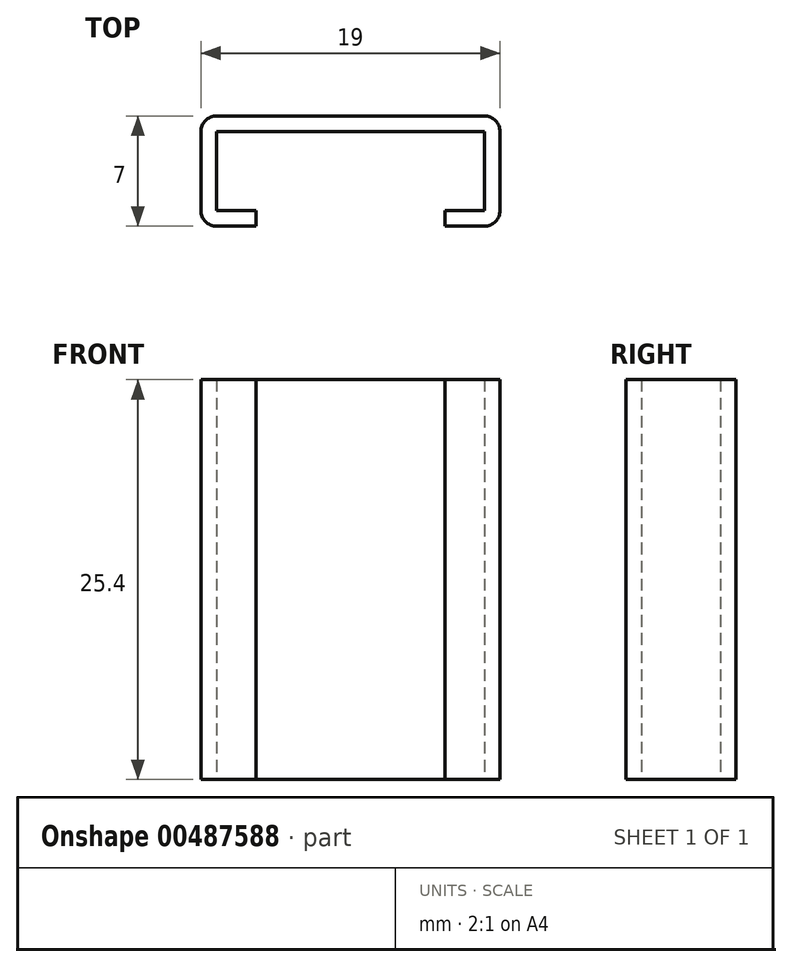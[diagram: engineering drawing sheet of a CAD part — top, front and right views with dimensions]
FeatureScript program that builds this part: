
annotation { "Feature Type Name" : "Feature", "Feature Type Description" : "" }
export const myFeature = defineFeature(function(context is Context, id is Id, definition is map)
    precondition{}
    {
        {
            var Q0;
            Q0=qCreatedBy(makeId("Top.planeOp"),FACE);
            var sketch = newSketch(context, id + "F0", { "sketchPlane" : qUnion([Q0])});
            skLineSegment(sketch, "E0", {"start": v(0, 0) * mm, "end": v(-8.5, 0) * mm});
            skLineSegment(sketch, "E1", {"start": v(-8.5, 0) * mm, "end": v(-8.5, -5) * mm});
            skLineSegment(sketch, "E2", {"start": v(-8.5, -5) * mm, "end": v(-6, -5) * mm});
            skLineSegment(sketch, "E3", {"start": v(0, 0) * mm, "end": v(0, 1) * mm});
            skLineSegment(sketch, "E4", {"start": v(0, 1) * mm, "end": v(-9.5, 1) * mm});
            skLineSegment(sketch, "E5", {"start": v(-9.5, 1) * mm, "end": v(-9.5, -6) * mm});
            skLineSegment(sketch, "E6", {"start": v(-9.5, -6) * mm, "end": v(-6, -6) * mm});
            skLineSegment(sketch, "E7", {"start": v(-6, -6) * mm, "end": v(-6, -5) * mm});
            skLineSegment(sketch, "E8.MirrorCS", {"start": v(9.5, 1) * mm, "end": v(9.5, -6) * mm});
            skLineSegment(sketch, "E9.MirrorCS", {"start": v(8.5, -5) * mm, "end": v(6, -5) * mm});
            skLineSegment(sketch, "E10.MirrorCS", {"start": v(0, 0) * mm, "end": v(8.5, 0) * mm});
            skLineSegment(sketch, "E11.MirrorCS", {"start": v(6, -6) * mm, "end": v(6, -5) * mm});
            skLineSegment(sketch, "E12.MirrorCS", {"start": v(0, 1) * mm, "end": v(9.5, 1) * mm});
            skLineSegment(sketch, "E13.MirrorCS", {"start": v(9.5, -6) * mm, "end": v(6, -6) * mm});
            skLineSegment(sketch, "E14.MirrorCS", {"start": v(8.5, 0) * mm, "end": v(8.5, -5) * mm});
            skSolve(sketch);
        }
        {
            var Q0;
            Q0=qSketchRegion(id+"F0",true);
            extrude(context, id + "F1", {"entities" : qUnion([Q0]), "depth" : 25.4 * mm});
        }
        {
            var Q0;
            Q0=makeQuery(id+"F1.opExtrude","SWEPT_EDGE",EDGE,{"disambiguationData":[OSD([sQuery(id+"F0.wireOp",EDGE,"E4"),sQuery(id+"F0.wireOp",EDGE,"E5")])]});
            var Q1;
            Q1=makeQuery(id+"F1.opExtrude","SWEPT_EDGE",EDGE,{"disambiguationData":[OSD([sQuery(id+"F0.wireOp",EDGE,"E8.MirrorCS"),sQuery(id+"F0.wireOp",EDGE,"E12.MirrorCS")])]});
            fillet(context, id + "F2", {"entities" : qUnion([Q0, Q1]), "radius" : 1 * mm, "tangentPropagation" : true, "allowEdgeOverflow" : false});
        }
        {
            var Q0;
            Q0=makeQuery(id+"F1.opExtrude","SWEPT_EDGE",EDGE,{"disambiguationData":[OSD([sQuery(id+"F0.wireOp",EDGE,"E5"),sQuery(id+"F0.wireOp",EDGE,"E6")])]});
            var Q1;
            Q1=makeQuery(id+"F1.opExtrude","SWEPT_EDGE",EDGE,{"disambiguationData":[OSD([sQuery(id+"F0.wireOp",EDGE,"E8.MirrorCS"),sQuery(id+"F0.wireOp",EDGE,"E13.MirrorCS")])]});
            fillet(context, id + "F3", {"entities" : qUnion([Q0, Q1]), "radius" : 1 * mm, "tangentPropagation" : true, "allowEdgeOverflow" : false});
        }
    });
